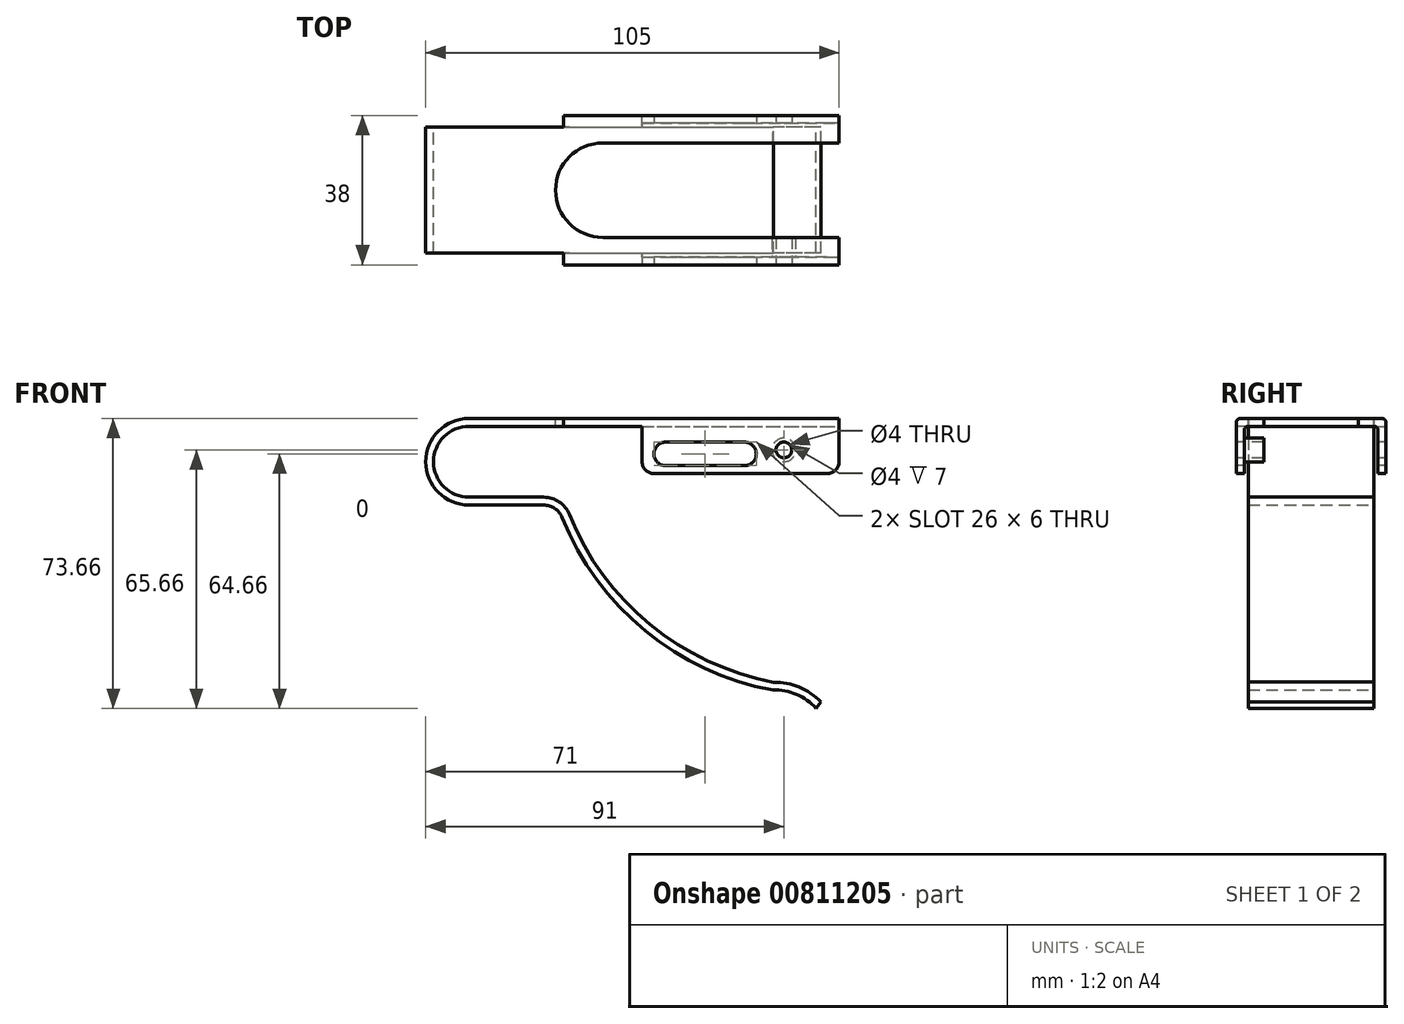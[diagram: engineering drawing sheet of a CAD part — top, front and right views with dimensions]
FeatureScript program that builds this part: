
annotation { "Feature Type Name" : "Feature", "Feature Type Description" : "" }
export const myFeature = defineFeature(function(context is Context, id is Id, definition is map)
    precondition{}
    {
        {
            var Q0;
            Q0=qCreatedBy(makeId("Front.planeOp"),FACE);
            var sketch = newSketch(context, id + "F0", { "sketchPlane" : qUnion([Q0])});
            skArc(sketch, "E0", {"start": v(0, 11) * mm, "mid": v(-11, 0) * mm, "end": v(0, -11) * mm});
            skLineSegment(sketch, "E1", {"start": v(0, 11) * mm, "end": v(94, 11) * mm});
            skLineSegment(sketch, "E2", {"start": v(0, -11) * mm, "end": v(19, -11) * mm});
            skArc(sketch, "E3", {"start": v(23.64, -14.13) * mm, "mid": v(44.8, -42.93) * mm, "end": v(77.2, -58) * mm});
            skArc(sketch, "E4", {"start": v(88.18, -62.66) * mm, "mid": v(83.21, -59.1) * mm, "end": v(77.2, -58) * mm});
            skPoint(sketch, "E5.visualSharp", {"position": v(22.46, -11) * mm});
            skArc(sketch, "E5.filletArc", {"start": v(23.64, -14.13) * mm, "mid": v(21.8, -11.86) * mm, "end": v(19, -11) * mm});
            skLineSegment(sketch, "E6.0", {"start": v(0, 9) * mm, "end": v(94, 9) * mm});
            skArc(sketch, "E6.1", {"start": v(0, 9) * mm, "mid": v(-9, 0) * mm, "end": v(0, -9) * mm});
            skArc(sketch, "E6.2", {"start": v(89.37, -61) * mm, "mid": v(83.9, -57.23) * mm, "end": v(77.36, -56) * mm});
            skArc(sketch, "E6.3", {"start": v(25.5, -13.38) * mm, "mid": v(45.99, -41.32) * mm, "end": v(77.36, -56) * mm});
            skArc(sketch, "E6.4", {"start": v(25.5, -13.38) * mm, "mid": v(22.92, -10.2) * mm, "end": v(19, -9) * mm});
            skLineSegment(sketch, "E6.5", {"start": v(0, -9) * mm, "end": v(19, -9) * mm});
            skLineSegment(sketch, "E7", {"start": v(94, 9) * mm, "end": v(94, 11) * mm});
            skLineSegment(sketch, "E8", {"start": v(89.37, -61) * mm, "end": v(88.18, -62.66) * mm});
            skSolve(sketch);
        }
        {
            var Q0;
            Q0 = qSketchRegion(id + "F0", true);
            extrude(context, id + "F1", {"entities" : qUnion([Q0]), "depth" : 16 * mm, "offsetDistance" : 25 * mm});
        }
        {
            var Q0;
            Q0=makeQuery(id+"F1.opExtrude","SWEPT_FACE",FACE,{"disambiguationData":[OSD([sQuery(id+"F0.wireOp",EDGE,"E1")])]});
            var sketch = newSketch(context, id + "F2", { "sketchPlane" : qUnion([Q0])});
            skLineSegment(sketch, "E9.bottom", {"start": v(94, -16) * mm, "end": v(24, -16) * mm});
            skLineSegment(sketch, "E9.top", {"start": v(94, -19) * mm, "end": v(24, -19) * mm});
            skLineSegment(sketch, "E9.left", {"start": v(94, -16) * mm, "end": v(94, -19) * mm});
            skLineSegment(sketch, "E9.right", {"start": v(24, -16) * mm, "end": v(24, -19) * mm});
            skSolve(sketch);
        }
        {
            var Q0;
            Q0 = qSketchRegion(id + "F2", true);
            extrude(context, id + "F3", {"entities" : qUnion([Q0]), "operationType" : NewBodyOperationType.ADD, "oppositeDirection" : true, "depth" : 2 * mm, "offsetDistance" : 25 * mm});
        }
        {
            var Q0;
            Q0=makeQuery(id+"F3.opExtrude","SWEPT_FACE",FACE,{"disambiguationData":[OSD([sQuery(id+"F2.wireOp",EDGE,"E9.top")])]});
            var sketch = newSketch(context, id + "F4", { "sketchPlane" : qUnion([Q0])});
            skLineSegment(sketch, "E10.bottom", {"start": v(94, 11) * mm, "end": v(44, 11) * mm});
            skLineSegment(sketch, "E10.top", {"start": v(94, -3) * mm, "end": v(44, -3) * mm});
            skLineSegment(sketch, "E10.left", {"start": v(94, 11) * mm, "end": v(94, -3) * mm});
            skLineSegment(sketch, "E10.right", {"start": v(44, 11) * mm, "end": v(44, -3) * mm});
            skSolve(sketch);
        }
        {
            var Q0;
            Q0 = qSketchRegion(id + "F4", true);
            extrude(context, id + "F5", {"entities" : qUnion([Q0]), "operationType" : NewBodyOperationType.ADD, "oppositeDirection" : true, "depth" : 2 * mm, "offsetDistance" : 25 * mm});
        }
        {
            var Q0;
            Q0=makeQuery(id+"F3.opExtrude","CAP_EDGE",EDGE,{"disambiguationData":[OSD([sQuery(id+"F2.wireOp",EDGE,"E9.top")])],"isStart":true});
            var Q1;
            Q1=makeQuery(id+"F5.boolean.opBoolean","INTERSECT",EDGE,{"derivedFrom":[makeQuery(id+"F3.boolean.opBoolean","MERGE",FACE,{"derivedFrom":[makeQuery(id+"F1.opExtrude","SWEPT_FACE",FACE,{"disambiguationData":[OSD([sQuery(id+"F0.wireOp",EDGE,"E6.0")])]}),makeQuery(id+"F3.opExtrude","CAP_FACE",FACE,{"disambiguationData":[OSD([sQuery(id+"F2.wireOp",EDGE,"E9.bottom"),sQuery(id+"F2.wireOp",EDGE,"E9.top"),sQuery(id+"F2.wireOp",EDGE,"E9.left"),sQuery(id+"F2.wireOp",EDGE,"E9.right")])],"isStart":false})]}),makeQuery(id+"F5.opExtrude","CAP_FACE",FACE,{"disambiguationData":[OSD([sQuery(id+"F4.wireOp",EDGE,"E10.bottom"),sQuery(id+"F4.wireOp",EDGE,"E10.top"),sQuery(id+"F4.wireOp",EDGE,"E10.left"),sQuery(id+"F4.wireOp",EDGE,"E10.right")])],"isStart":false})]});
            fillet(context, id + "F6", {"entities" : qUnion([Q0, Q1]), "radius" : 1 * mm, "tangentPropagation" : true, "allowEdgeOverflow" : false});
        }
        {
            var Q0;
            Q0=makeQuery(id+"F1.opExtrude","SWEPT_BODY",BODY,{"disambiguationData":[OSD([sQuery(id+"F0.wireOp",EDGE,"E0"),sQuery(id+"F0.wireOp",EDGE,"E1"),sQuery(id+"F0.wireOp",EDGE,"E2"),sQuery(id+"F0.wireOp",EDGE,"E3"),sQuery(id+"F0.wireOp",EDGE,"E4"),sQuery(id+"F0.wireOp",EDGE,"E5.filletArc"),sQuery(id+"F0.wireOp",EDGE,"E6.0"),sQuery(id+"F0.wireOp",EDGE,"E6.1"),sQuery(id+"F0.wireOp",EDGE,"E6.2"),sQuery(id+"F0.wireOp",EDGE,"E6.3"),sQuery(id+"F0.wireOp",EDGE,"E6.4"),sQuery(id+"F0.wireOp",EDGE,"E6.5"),sQuery(id+"F0.wireOp",EDGE,"E7"),sQuery(id+"F0.wireOp",EDGE,"E8")])]});
            var Q1;
            Q1=qCreatedBy(makeId("Front.planeOp"),FACE);
            mirror(context, id + "F7", {"operationType" : NewBodyOperationType.ADD, "entities" : qUnion([Q0]), "mirrorPlane" : qUnion([Q1])});
        }
        {
            var Q0;
            {var subQ0=makeQuery(id+"F3.boolean.opBoolean","MERGE",FACE,{"derivedFrom":[makeQuery(id+"F1.opExtrude","SWEPT_FACE",FACE,{"disambiguationData":[OSD([sQuery(id+"F0.wireOp",EDGE,"E1")])]}),makeQuery(id+"F3.opExtrude","CAP_FACE",FACE,{"disambiguationData":[OSD([sQuery(id+"F2.wireOp",EDGE,"E9.bottom"),sQuery(id+"F2.wireOp",EDGE,"E9.top"),sQuery(id+"F2.wireOp",EDGE,"E9.left"),sQuery(id+"F2.wireOp",EDGE,"E9.right")])],"isStart":true})]});Q0=makeQuery(id+"F7.boolean.opBoolean","MERGE",FACE,{"derivedFrom":[subQ0,makeQuery(id+"F7.opPattern","COPY",FACE,{"derivedFrom":subQ0,"instanceName":"1"})]});}
            var sketch = newSketch(context, id + "F8", { "sketchPlane" : qUnion([Q0])});
            skArc(sketch, "E11", {"start": v(34, 12) * mm, "mid": v(22, 0) * mm, "end": v(34, -12) * mm});
            skLineSegment(sketch, "E12", {"start": v(34, 12) * mm, "end": v(94, 12) * mm});
            skLineSegment(sketch, "E13", {"start": v(34, -12) * mm, "end": v(94, -12) * mm});
            skLineSegment(sketch, "E14", {"start": v(94, -12) * mm, "end": v(94, 12) * mm});
            skSolve(sketch);
        }
        {
            var Q0;
            Q0 = qSketchRegion(id + "F8", true);
            extrude(context, id + "F9", {"entities" : qUnion([Q0]), "operationType" : NewBodyOperationType.REMOVE, "oppositeDirection" : true, "depth" : 2 * mm, "offsetDistance" : 25 * mm});
        }
        {
            var Q0;
            Q0=makeQuery(id+"F5.boolean.opBoolean","MERGE",FACE,{"derivedFrom":[makeQuery(id+"F3.opExtrude","SWEPT_FACE",FACE,{"disambiguationData":[OSD([sQuery(id+"F2.wireOp",EDGE,"E9.top")])]}),makeQuery(id+"F5.opExtrude","CAP_FACE",FACE,{"disambiguationData":[OSD([sQuery(id+"F4.wireOp",EDGE,"E10.bottom"),sQuery(id+"F4.wireOp",EDGE,"E10.top"),sQuery(id+"F4.wireOp",EDGE,"E10.left"),sQuery(id+"F4.wireOp",EDGE,"E10.right")])],"isStart":true})]});
            var sketch = newSketch(context, id + "F10", { "sketchPlane" : qUnion([Q0])});
            skLineSegment(sketch, "E15", {"start": v(50, 2) * mm, "end": v(70, 2) * mm});
            skArc(sketch, "E16.0.startCap", {"start": v(50, -1) * mm, "mid": v(47, 2) * mm, "end": v(50, 5) * mm});
            skArc(sketch, "E16.0.endCap", {"start": v(70, 5) * mm, "mid": v(73, 2) * mm, "end": v(70, -1) * mm});
            skLineSegment(sketch, "E16.0.left", {"start": v(50, 5) * mm, "end": v(70, 5) * mm});
            skLineSegment(sketch, "E16.0.right", {"start": v(50, -1) * mm, "end": v(70, -1) * mm});
            skSolve(sketch);
        }
        {
            var Q0;
            Q0 = qSketchRegion(id + "F10", true);
            extrude(context, id + "F11", {"entities" : qUnion([Q0]), "operationType" : NewBodyOperationType.REMOVE, "endBound" : BoundingType.THROUGH_ALL, "oppositeDirection" : true, "depth" : 25 * mm, "offsetDistance" : 25 * mm});
        }
        {
            var Q0;
            Q0=makeQuery(id+"F5.boolean.opBoolean","MERGE",FACE,{"derivedFrom":[makeQuery(id+"F3.opExtrude","SWEPT_FACE",FACE,{"disambiguationData":[OSD([sQuery(id+"F2.wireOp",EDGE,"E9.top")])]}),makeQuery(id+"F5.opExtrude","CAP_FACE",FACE,{"disambiguationData":[OSD([sQuery(id+"F4.wireOp",EDGE,"E10.bottom"),sQuery(id+"F4.wireOp",EDGE,"E10.top"),sQuery(id+"F4.wireOp",EDGE,"E10.left"),sQuery(id+"F4.wireOp",EDGE,"E10.right")])],"isStart":true})]});
            var sketch = newSketch(context, id + "F12", { "sketchPlane" : qUnion([Q0])});
            skPoint(sketch, "E17", {"position": v(80, 3) * mm});
            skSolve(sketch);
        }
        {
            var Q0;
            Q0=sQuery(id+"F12.wireOp",VERTEX,"E17");
            var Q1;
            Q1=makeQuery(id+"F1.opExtrude","SWEPT_BODY",BODY,{"disambiguationData":[OSD([sQuery(id+"F0.wireOp",EDGE,"E0"),sQuery(id+"F0.wireOp",EDGE,"E1"),sQuery(id+"F0.wireOp",EDGE,"E2"),sQuery(id+"F0.wireOp",EDGE,"E3"),sQuery(id+"F0.wireOp",EDGE,"E4"),sQuery(id+"F0.wireOp",EDGE,"E5.filletArc"),sQuery(id+"F0.wireOp",EDGE,"E6.0"),sQuery(id+"F0.wireOp",EDGE,"E6.1"),sQuery(id+"F0.wireOp",EDGE,"E6.2"),sQuery(id+"F0.wireOp",EDGE,"E6.3"),sQuery(id+"F0.wireOp",EDGE,"E6.4"),sQuery(id+"F0.wireOp",EDGE,"E6.5"),sQuery(id+"F0.wireOp",EDGE,"E7"),sQuery(id+"F0.wireOp",EDGE,"E8")])]});
            hole(context, id + "F13", {"style" : HoleStyle.SIMPLE, "endStyle" : HoleEndStyle.THROUGH, "holeDiameter" : 4 * mm, "majorDiameter" : 5 * mm, "isTappedThrough" : true, "tappedDepth" : 12 * mm, "tapClearance" : 3, "locations" : qUnion([Q0]), "scope" : qUnion([Q1])});
        }
        {
            var Q0;
            Q0=makeQuery(id+"F5.opExtrude","CAP_FACE",FACE,{"disambiguationData":[OSD([sQuery(id+"F4.wireOp",EDGE,"E10.bottom"),sQuery(id+"F4.wireOp",EDGE,"E10.top"),sQuery(id+"F4.wireOp",EDGE,"E10.left"),sQuery(id+"F4.wireOp",EDGE,"E10.right")])],"isStart":false});
            var sketch = newSketch(context, id + "F14", { "sketchPlane" : qUnion([Q0])});
            skCircle(sketch, "E18.0", {"center": v(-80, 3) * mm, "radius": 2 * mm});
            skCircle(sketch, "E19.0", {"center": v(-80, 3) * mm, "radius": 3 * mm});
            skSolve(sketch);
        }
        {
            var Q0;
            Q0=makeQuery(id+"F14.imprint","IMPRINT",FACE,{"disambiguationData":[TD([[makeQuery(id+"F14.imprint","IMPRINT",EDGE,{"derivedFrom":sQuery(id+"F14.wireOp",EDGE,"E18.0")}),-1.0]])]});
            extrude(context, id + "F15", {"entities" : qUnion([Q0]), "operationType" : NewBodyOperationType.ADD, "depth" : 5 * mm, "offsetDistance" : 25 * mm});
        }
        {
            var Q0;
            Q0=makeQuery(id+"F5.opExtrude","SWEPT_EDGE",EDGE,{"disambiguationData":[OSD([sQuery(id+"F4.wireOp",EDGE,"E10.top"),sQuery(id+"F4.wireOp",EDGE,"E10.right")])]});
            var Q1;
            Q1=makeQuery(id+"F7.opPattern","COPY",EDGE,{"derivedFrom":makeQuery(id+"F5.opExtrude","SWEPT_EDGE",EDGE,{"disambiguationData":[OSD([sQuery(id+"F4.wireOp",EDGE,"E10.top"),sQuery(id+"F4.wireOp",EDGE,"E10.right")])]}),"instanceName":"1"});
            var Q2;
            Q2=makeQuery(id+"F5.opExtrude","SWEPT_EDGE",EDGE,{"disambiguationData":[OSD([sQuery(id+"F4.wireOp",EDGE,"E10.top"),sQuery(id+"F4.wireOp",EDGE,"E10.left")])]});
            var Q3;
            Q3=makeQuery(id+"F7.opPattern","COPY",EDGE,{"derivedFrom":makeQuery(id+"F5.opExtrude","SWEPT_EDGE",EDGE,{"disambiguationData":[OSD([sQuery(id+"F4.wireOp",EDGE,"E10.top"),sQuery(id+"F4.wireOp",EDGE,"E10.left")])]}),"instanceName":"1"});
            fillet(context, id + "F16", {"entities" : qUnion([Q0, Q1, Q2, Q3]), "radius" : 3 * mm, "tangentPropagation" : true, "allowEdgeOverflow" : false});
        }
    });
